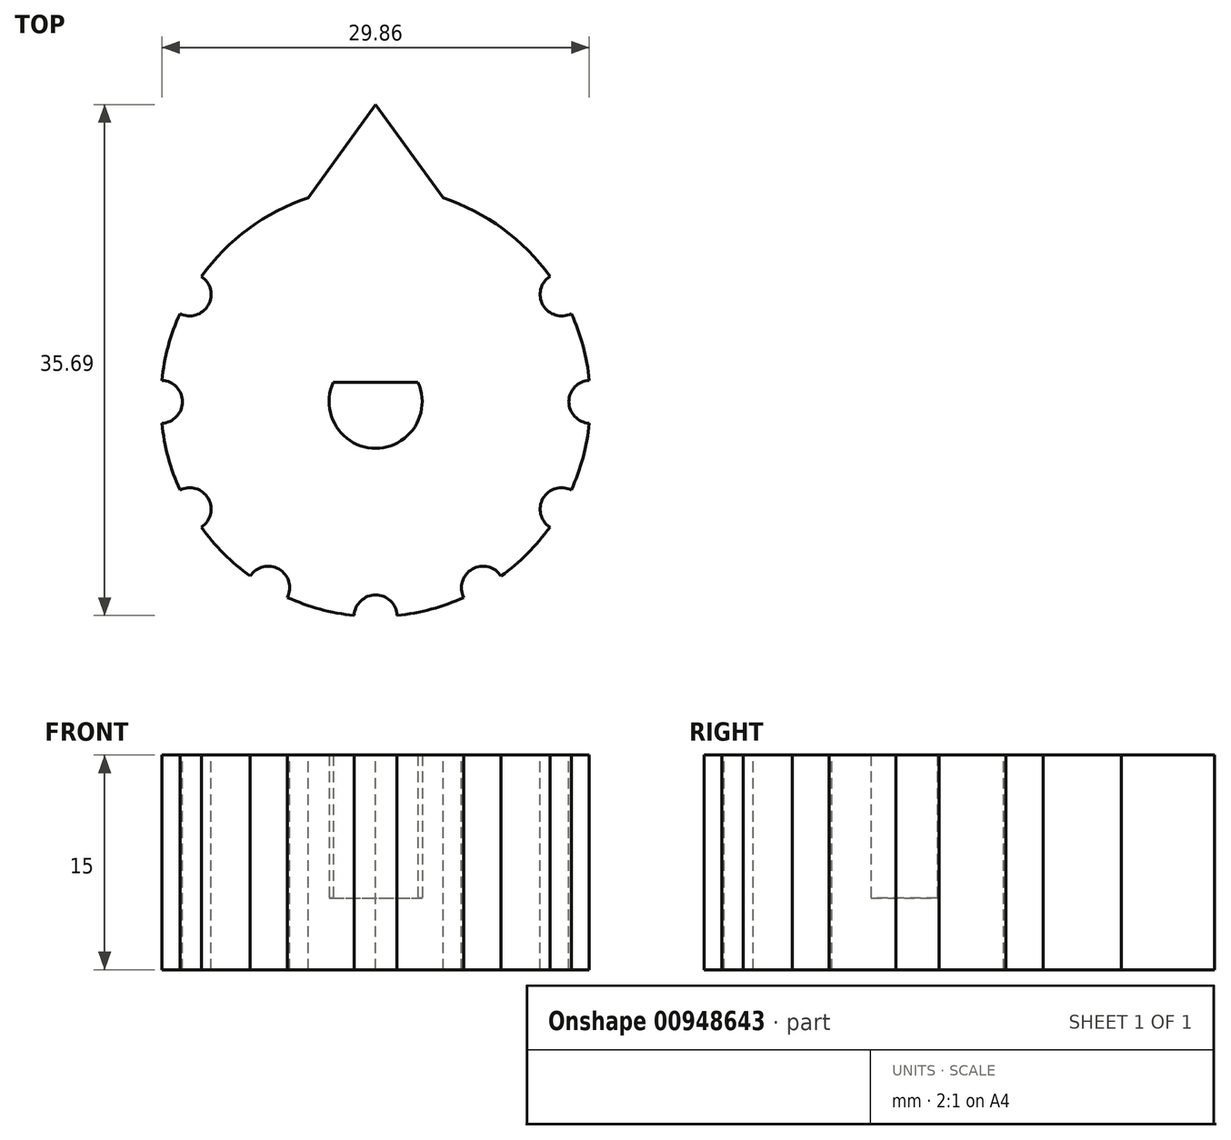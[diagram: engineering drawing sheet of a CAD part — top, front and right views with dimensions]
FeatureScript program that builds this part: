
annotation { "Feature Type Name" : "Feature", "Feature Type Description" : "" }
export const myFeature = defineFeature(function(context is Context, id is Id, definition is map)
    precondition{}
    {
        {
            var Q0;
            Q0=qCreatedBy(makeId("Top.planeOp"),FACE);
            var sketch = newSketch(context, id + "F0", { "sketchPlane" : qUnion([Q0])});
            skCircle(sketch, "E0", {"center": v(0, 0) * mm, "radius": 15 * mm});
            skArc(sketch, "E1", {"start": v(-2.95, 1.36) * mm, "mid": v(0, -3.25) * mm, "end": v(2.95, 1.36) * mm});
            skLineSegment(sketch, "E2.top", {"start": v(-2.95, 1.36) * mm, "end": v(2.95, 1.36) * mm});
            skSolve(sketch);
        }
        {
            var Q0;
            Q0=makeQuery(id+"F0.imprint","IMPRINT",FACE,{"disambiguationData":[TD([[makeQuery(id+"F0.imprint","IMPRINT",EDGE,{"derivedFrom":sQuery(id+"F0.wireOp",EDGE,"E0")}),1.0]])]});
            extrude(context, id + "F1", {"entities" : qUnion([Q0]), "depth" : 10 * mm, "offsetDistance" : 25 * mm});
        }
        {
            var Q0;
            Q0=makeQuery(id+"F1.opExtrude","CAP_FACE",FACE,{"disambiguationData":[OSD([sQuery(id+"F0.wireOp",EDGE,"E0"),sQuery(id+"F0.wireOp",EDGE,"E1"),sQuery(id+"F0.wireOp",EDGE,"E2.top")])],"isStart":true});
            var sketch = newSketch(context, id + "F2", { "sketchPlane" : qUnion([Q0])});
            skCircle(sketch, "E3", {"center": v(0, 0) * mm, "radius": 15 * mm});
            skSolve(sketch);
        }
        {
            var Q0;
            Q0=makeQuery(id+"F2.imprint","IMPRINT",FACE,{"disambiguationData":[TD([[makeQuery(id+"F2.imprint","IMPRINT",EDGE,{"derivedFrom":makeQuery(id+"F1.opExtrude","CAP_EDGE",EDGE,{"disambiguationData":[OSD([sQuery(id+"F0.wireOp",EDGE,"E1")])],"isStart":true})}),-1.0]])]});
            var Q1;
            Q1=makeQuery(id+"F2.imprint","IMPRINT",FACE,{"disambiguationData":[TD([[makeQuery(id+"F2.imprint","IMPRINT",EDGE,{"derivedFrom":sQuery(id+"F2.wireOp",EDGE,"E3")}),-1.0]])]});
            extrude(context, id + "F3", {"entities" : qUnion([Q0, Q1]), "operationType" : NewBodyOperationType.ADD, "depth" : 5 * mm, "offsetDistance" : 25 * mm});
        }
        {
            var Q0;
            Q0=makeQuery(id+"F1.opExtrude","CAP_FACE",FACE,{"disambiguationData":[OSD([sQuery(id+"F0.wireOp",EDGE,"E0"),sQuery(id+"F0.wireOp",EDGE,"E1"),sQuery(id+"F0.wireOp",EDGE,"E2.top")])],"isStart":false});
            var sketch = newSketch(context, id + "F4", { "sketchPlane" : qUnion([Q0])});
            skLineSegment(sketch, "E4", {"start": v(0, 20.76) * mm, "end": v(-4.7, 14.24) * mm});
            skLineSegment(sketch, "E5", {"start": v(4.7, 14.24) * mm, "end": v(0, 20.76) * mm});
            skPoint(sketch, "E6.orphan", {"position": v(-15, 0) * mm});
            skPoint(sketch, "E7.orphan", {"position": v(15, 0) * mm});
            skArc(sketch, "E8", {"start": v(1.5, -14.93) * mm, "mid": v(0, -13.5) * mm, "end": v(-1.5, -14.93) * mm});
            skCircle(sketch, "E9", {"center": v(0, 0) * mm, "radius": 15 * mm});
            skArc(sketch, "E10.1.0", {"start": v(8.76, -12.18) * mm, "mid": v(6.75, -11.7) * mm, "end": v(6.17, -13.67) * mm});
            skArc(sketch, "E10.2.0", {"start": v(13.67, -6.17) * mm, "mid": v(11.7, -6.75) * mm, "end": v(12.18, -8.76) * mm});
            skArc(sketch, "E10.3.0", {"start": v(14.93, 1.5) * mm, "mid": v(13.5, 0) * mm, "end": v(14.93, -1.5) * mm});
            skArc(sketch, "E10.4.0", {"start": v(12.18, 8.76) * mm, "mid": v(11.7, 6.75) * mm, "end": v(13.67, 6.17) * mm});
            skArc(sketch, "E10.8.0", {"start": v(-13.67, 6.17) * mm, "mid": v(-11.7, 6.75) * mm, "end": v(-12.18, 8.76) * mm});
            skArc(sketch, "E10.9.0", {"start": v(-14.93, -1.5) * mm, "mid": v(-13.5, 0) * mm, "end": v(-14.93, 1.5) * mm});
            skArc(sketch, "E10.10.0", {"start": v(-12.18, -8.76) * mm, "mid": v(-11.7, -6.75) * mm, "end": v(-13.67, -6.17) * mm});
            skArc(sketch, "E10.11.0", {"start": v(-6.17, -13.67) * mm, "mid": v(-6.75, -11.7) * mm, "end": v(-8.76, -12.18) * mm});
            skSolve(sketch);
        }
        {
            var Q0;
            {var subQ0=sQuery(id+"F4.wireOp",EDGE,"E4");Q0=makeQuery(id+"F4.imprint","IMPRINT",FACE,{"disambiguationData":[TD([[makeQuery(id+"F4.imprint","IMPRINT",EDGE,{"derivedFrom":subQ0}),1.0]])]});}
            extrude(context, id + "F5", {"entities" : qUnion([Q0]), "operationType" : NewBodyOperationType.ADD, "oppositeDirection" : true, "depth" : 15 * mm, "offsetDistance" : 25 * mm});
        }
        {
            var Q0;
            {var subQ0=sQuery(id+"F4.wireOp",EDGE,"E10.7.0");Q0=makeQuery(id+"F4.imprint","IMPRINT",FACE,{"disambiguationData":[TD([[makeQuery(id+"F4.imprint","IMPRINT",EDGE,{"derivedFrom":subQ0}),1.0]])]});}
            var Q1;
            {var subQ0=sQuery(id+"F4.wireOp",EDGE,"E10.5.0");Q1=makeQuery(id+"F4.imprint","IMPRINT",FACE,{"disambiguationData":[TD([[makeQuery(id+"F4.imprint","IMPRINT",EDGE,{"derivedFrom":subQ0}),1.0]])]});}
            var Q2;
            {var subQ0=sQuery(id+"F4.wireOp",EDGE,"E10.4.0");Q2=makeQuery(id+"F4.imprint","IMPRINT",FACE,{"disambiguationData":[TD([[makeQuery(id+"F4.imprint","IMPRINT",EDGE,{"derivedFrom":subQ0}),1.0]])]});}
            var Q3;
            {var subQ0=sQuery(id+"F4.wireOp",EDGE,"E10.3.0");Q3=makeQuery(id+"F4.imprint","IMPRINT",FACE,{"disambiguationData":[TD([[makeQuery(id+"F4.imprint","IMPRINT",EDGE,{"derivedFrom":subQ0}),1.0]])]});}
            var Q4;
            {var subQ0=sQuery(id+"F4.wireOp",EDGE,"E10.2.0");Q4=makeQuery(id+"F4.imprint","IMPRINT",FACE,{"disambiguationData":[TD([[makeQuery(id+"F4.imprint","IMPRINT",EDGE,{"derivedFrom":subQ0}),1.0]])]});}
            var Q5;
            {var subQ0=sQuery(id+"F4.wireOp",EDGE,"E10.1.0");Q5=makeQuery(id+"F4.imprint","IMPRINT",FACE,{"disambiguationData":[TD([[makeQuery(id+"F4.imprint","IMPRINT",EDGE,{"derivedFrom":subQ0}),1.0]])]});}
            var Q6;
            {var subQ0=sQuery(id+"F4.wireOp",EDGE,"E8");Q6=makeQuery(id+"F4.imprint","IMPRINT",FACE,{"disambiguationData":[TD([[makeQuery(id+"F4.imprint","IMPRINT",EDGE,{"derivedFrom":subQ0}),1.0]])]});}
            var Q7;
            {var subQ0=sQuery(id+"F4.wireOp",EDGE,"E10.11.0");Q7=makeQuery(id+"F4.imprint","IMPRINT",FACE,{"disambiguationData":[TD([[makeQuery(id+"F4.imprint","IMPRINT",EDGE,{"derivedFrom":subQ0}),1.0]])]});}
            var Q8;
            {var subQ0=sQuery(id+"F4.wireOp",EDGE,"E10.10.0");Q8=makeQuery(id+"F4.imprint","IMPRINT",FACE,{"disambiguationData":[TD([[makeQuery(id+"F4.imprint","IMPRINT",EDGE,{"derivedFrom":subQ0}),1.0]])]});}
            var Q9;
            {var subQ0=sQuery(id+"F4.wireOp",EDGE,"E10.9.0");Q9=makeQuery(id+"F4.imprint","IMPRINT",FACE,{"disambiguationData":[TD([[makeQuery(id+"F4.imprint","IMPRINT",EDGE,{"derivedFrom":subQ0}),1.0]])]});}
            var Q10;
            {var subQ0=sQuery(id+"F4.wireOp",EDGE,"E10.8.0");Q10=makeQuery(id+"F4.imprint","IMPRINT",FACE,{"disambiguationData":[TD([[makeQuery(id+"F4.imprint","IMPRINT",EDGE,{"derivedFrom":subQ0}),1.0]])]});}
            extrude(context, id + "F6", {"entities" : qUnion([Q0, Q1, Q2, Q3, Q4, Q5, Q6, Q7, Q8, Q9, Q10]), "operationType" : NewBodyOperationType.REMOVE, "endBound" : BoundingType.UP_TO_NEXT, "oppositeDirection" : true, "depth" : 25 * mm, "offsetDistance" : 25 * mm});
        }
    });
